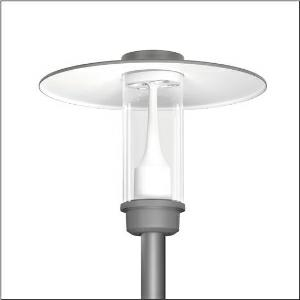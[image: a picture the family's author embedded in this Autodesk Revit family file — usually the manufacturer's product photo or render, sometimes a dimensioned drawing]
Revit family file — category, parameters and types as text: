
# Revit family: litepole_2_iq___st1_2a_5xa5425mf14h_5009
name_source: partatom
category: Lighting Fixtures
units: mm (PartAtom-declared; Revit-internal decimal feet)

## family parameters
Cut with Voids When Loaded = No
Host = Face
Light Source = No
Part Type = Normal
Room Calculation Point = No
Round Connector Dimension = Use Diameter
Shared = No

## types (1)
- --- (1 x LED, 1550 lm, 11.8 W, 2700K)
    Apparent Load = 12 VA
    CIE Flux Codes = 22 60 92 98 100
    Color Rendering = 70
    Color Temperature = 2700K
    Default Elevation = 1800 mm
    Description = Litepole 2 iQ, mast luminaire, Module 540 iQ-SR, primary light control with 3 zone facetted reflector, of plastic, silver coated, highly specular, structured, primary optical cover: cover, of PMMA, transparent, light distribution: ST1.2a, light emission: direct distribution, primary light characteristic: asymmetric, installation type: post-top, LED, High Power LED, rated luminous flux: 1.550lm, luminous efficacy: 131lm/W, light colour: 727, colour temperature: 2700K, control gear: iQ Street-Remote, control: pre-setting: logarithmic dimming characteristic, Street-Remote, Auto-Match, Temp-Guard, Lumen-Switch, Night-Set, Smart-Wire, Light-Fading, Desk-Remote (wireless, voltage-free reading and setting of iQ features in the workshop via application-optimized NFC function/RFID function), optimised constant luminous flux control (CLO 2.0), with terminal, 6-pole, max. 2.5mm², mains connection: 230..240V, AC, 50/60Hz, start of lifetime: 12W, end of service life: 12W, reduction: 6W, luminaire housing, upper part, of aluminium, coated, Siteco® metallic grey (DB 702S), diameter: 750mm, height: 590mm, spigot size: d x l = 76 x 70mm (post-top) | with reducer (optional accessory) 60 x 70mm, mounting height: 3..5m, post-top mast mounting element, of diecast aluminium, coated, Siteco® metallic grey (DB 702S), Module 540 iQ-SR, traffic white (RAL 9016), equipment: standard, protection rating (complete): IP65, insulation class (complete): insulation class II (safety insulation), certification: CE, ENEC, VDE, packaging unit: 1 piece

Light Distribution: ST1.2a
    Height = 590 mm
    Lamp = 1 x LED
    Lamp Light Flux = 1550 lm
    Lamp Power = 11.8 W
    Lamp count = 1
    Length = 750 mm
    Luminous efficacy = 131 lm/W
    Manufacturer = Siteco
    ModVariant = No
    Model = 5XA5425MF14H
    Number of Poles = 1
    OnlyDefault = Yes
    Power Factor = 1
    Product Name = Litepole 2 iQ | ST1.2a
    Product group = mast luminaire | pylon top
    ProductGroupID = 6100
    Protection Class = Protection class II
    Protection Degree = IP 65
    RLX_Detail_Level = 1
    RLX_Emergency_Light_Flux = 0 lm
    RLX_Emergency_Type = 0
    RLX_Emergency_Type_DB = No
    RlxData = <blob elided: 63801 chars, md5=5b08d750>
    Socket = socket
    Standby Power = 0 W
    System Light Flux = 1550 lm
    System Power = 12 W
    Type Comments = factory setting: luminous flux: 100 % | dim-lin: 254 | 472 mA
    Type Image = l_1006518.jpg
    URL = http://relux.com
    VarID = @adj_151925
    Voltage = 0 V
    Weight = 0.00 kg
    Width = 0 mm  [stored 0 ft]

note: [stored X ft] marks values corroborated as IEEE doubles in the binary element streams (Revit-internal decimal feet)

## geometry (parser evidence)
native form markers: Blend x4, Sweep x7
no freeform markers — native parametric forms only
